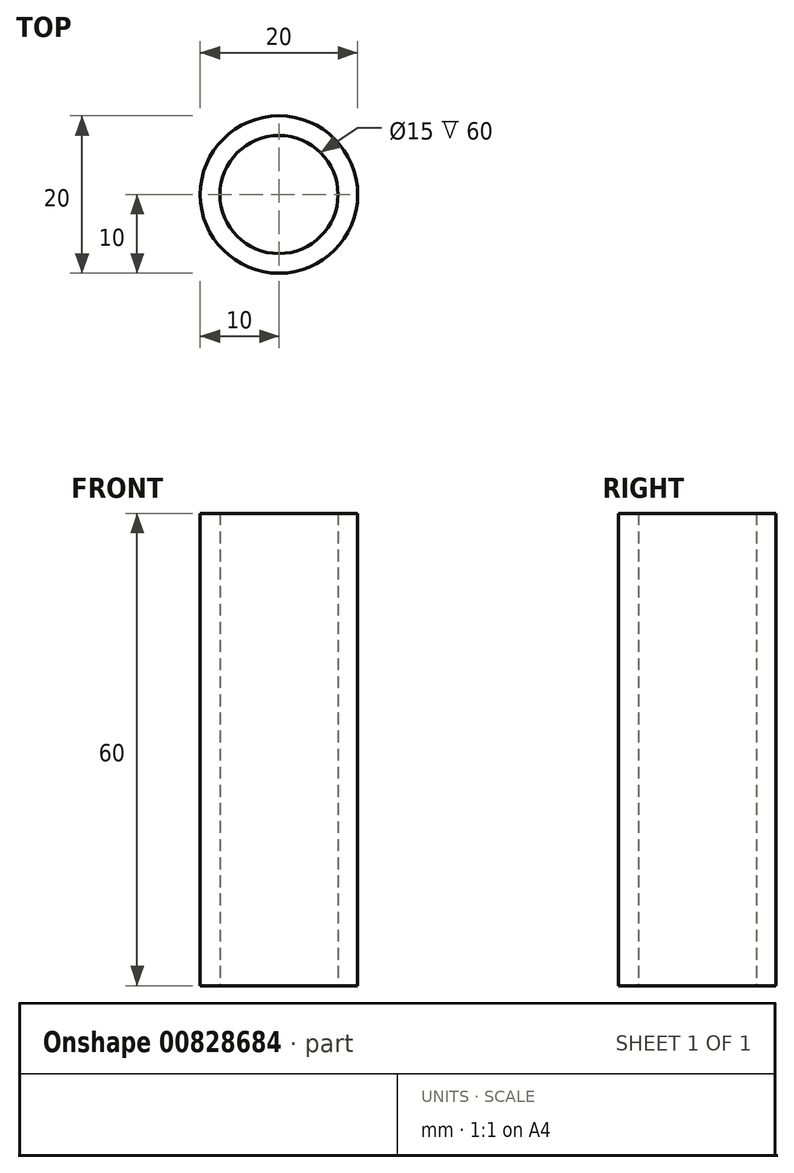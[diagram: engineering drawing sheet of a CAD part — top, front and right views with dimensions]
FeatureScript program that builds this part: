
annotation { "Feature Type Name" : "Feature", "Feature Type Description" : "" }
export const myFeature = defineFeature(function(context is Context, id is Id, definition is map)
    precondition{}
    {
        {
            var Q0;
            Q0=qCreatedBy(makeId("Top.planeOp"),FACE);
            var sketch = newSketch(context, id + "F0", { "sketchPlane" : qUnion([Q0])});
            skCircle(sketch, "E0", {"center": v(0, 0) * mm, "radius": 10 * mm});
            skCircle(sketch, "E1", {"center": v(0, 0) * mm, "radius": 7.5 * mm});
            skSolve(sketch);
        }
        {
            var Q0;
            Q0=makeQuery(id+"F0.imprint","IMPRINT",FACE,{"disambiguationData":[TD([[makeQuery(id+"F0.imprint","IMPRINT",EDGE,{"derivedFrom":sQuery(id+"F0.wireOp",EDGE,"E0")}),1.0]])]});
            extrude(context, id + "F1", {"entities" : qUnion([Q0]), "depth" : 60 * mm, "offsetDistance" : 25.4 * mm});
        }
    });
